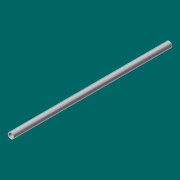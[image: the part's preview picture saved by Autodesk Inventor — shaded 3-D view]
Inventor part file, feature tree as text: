
AUTODESK INVENTOR PART (.ipt)
format: ipt  version: 2017 (Build 210142000, 142)  size: 93,184 bytes
history: native  units: in
note: dims shown in document units (in); Inventor stores cm internally (conversion verified against a paired STEP export)
features: extrude x1, sketch x1
ambient origin geometry x8: Origin, YZ Plane, XZ Plane, XY Plane, X Axis, Y Axis, Z Axis, Center Point
bodies: Solid1 (feature_tree)
feature tree (2):
  extrude  "Extrusion1"  Depth=78.25in
  sketch  "Sketch1"  dims[d0=2.875in d1=2.469in d2=78.25in d3=0.0in]
